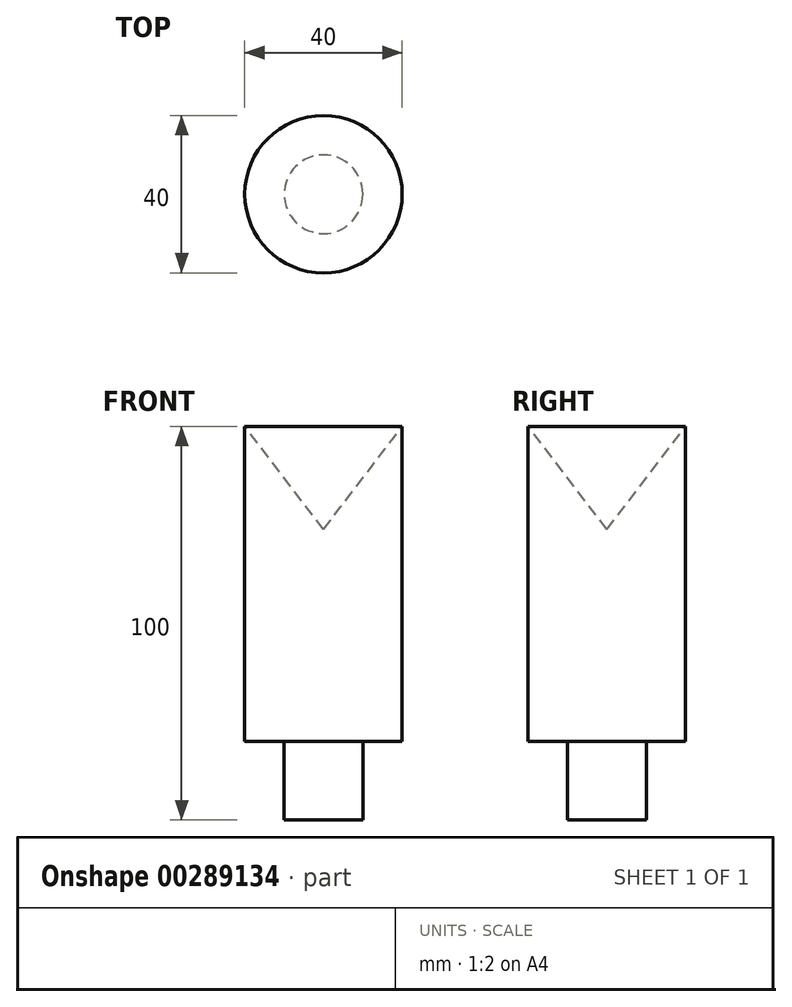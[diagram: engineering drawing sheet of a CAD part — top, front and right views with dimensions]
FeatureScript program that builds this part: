
annotation { "Feature Type Name" : "Feature", "Feature Type Description" : "" }
export const myFeature = defineFeature(function(context is Context, id is Id, definition is map)
    precondition{}
    {
        {
            var Q0;
            Q0=qCreatedBy(makeId("Front.planeOp"),FACE);
            var sketch = newSketch(context, id + "F0", { "sketchPlane" : qUnion([Q0])});
            skLineSegment(sketch, "E0", {"start": v(0, 29.91) * mm, "end": v(0, -43.88) * mm});
            skLineSegment(sketch, "E1", {"start": v(0, -43.88) * mm, "end": v(-10, -43.88) * mm});
            skLineSegment(sketch, "E2", {"start": v(-10, -43.88) * mm, "end": v(-10, -23.88) * mm});
            skLineSegment(sketch, "E3", {"start": v(-10, -23.88) * mm, "end": v(-20, -23.88) * mm});
            skLineSegment(sketch, "E4", {"start": v(-20, -23.88) * mm, "end": v(-20, 56.12) * mm});
            skLineSegment(sketch, "E5", {"start": v(-20, 56.12) * mm, "end": v(0, 29.91) * mm});
            skPoint(sketch, "E6.end.orphan", {"position": v(0, 46.95) * mm});
            skPoint(sketch, "E6.start.orphan", {"position": v(0, 55.57) * mm});
            skSolve(sketch);
        }
        {
            var Q0;
            Q0=makeQuery(id+"F0.imprint","IMPRINT",FACE,{"disambiguationData":[TD([[makeQuery(id+"F0.imprint","IMPRINT",EDGE,{"derivedFrom":sQuery(id+"F0.wireOp",EDGE,"E0")}),-1.0]])]});
            var Q1;
            Q1=sQuery(id+"F0.wireOp",EDGE,"E0");
            revolve(context, id + "F1", {"entities" : qUnion([Q0]), "axis" : qUnion([Q1]), "revolveType" : RevolveType.FULL});
        }
    });
